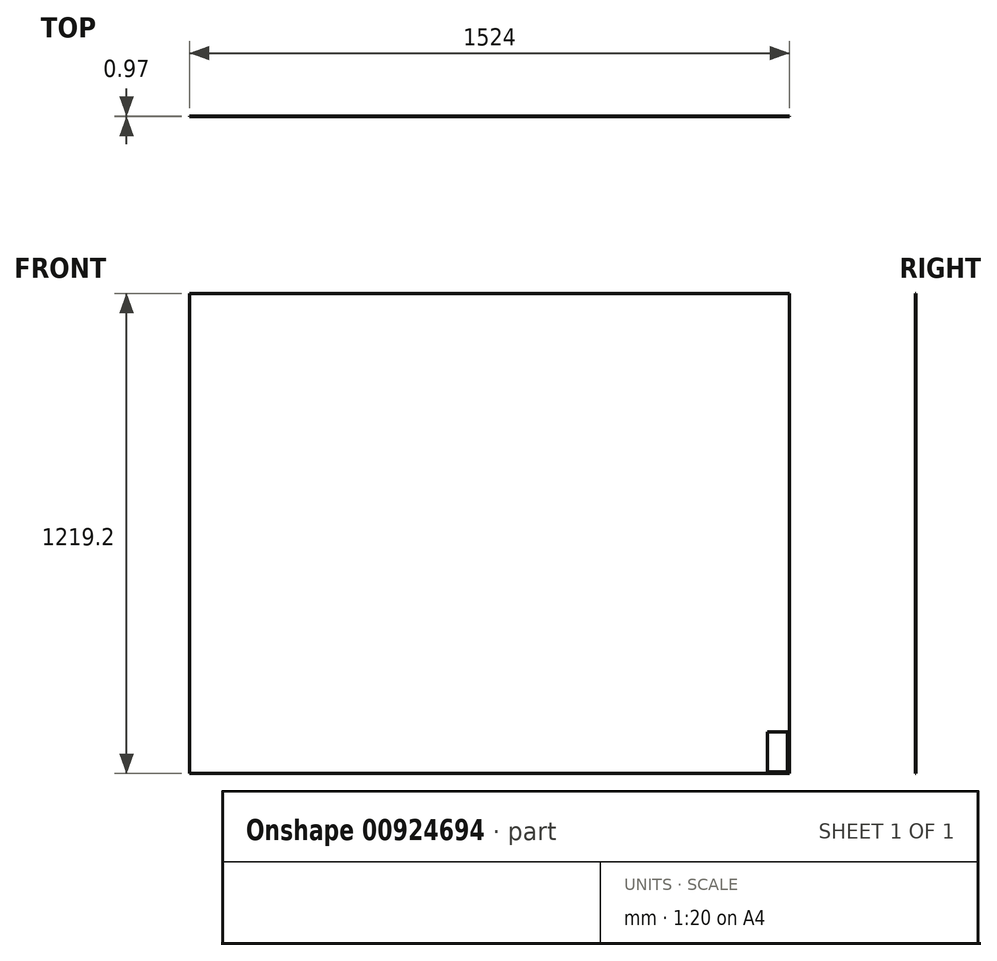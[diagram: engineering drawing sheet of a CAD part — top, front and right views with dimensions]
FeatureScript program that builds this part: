
annotation { "Feature Type Name" : "Feature", "Feature Type Description" : "" }
export const myFeature = defineFeature(function(context is Context, id is Id, definition is map)
    precondition{}
    {
        {
            var Q0;
            Q0=qCreatedBy(makeId("Front.planeOp"),FACE);
            var sketch = newSketch(context, id + "F0", { "sketchPlane" : qUnion([Q0])});
            skLineSegment(sketch, "E0.bottom", {"start": v(-1521.28, 1219.29) * mm, "end": v(2.72, 1219.29) * mm});
            skLineSegment(sketch, "E0.top", {"start": v(-1521.28, 0.09) * mm, "end": v(2.72, 0.09) * mm});
            skLineSegment(sketch, "E0.left", {"start": v(-1521.28, 1219.29) * mm, "end": v(-1521.28, 0.09) * mm});
            skLineSegment(sketch, "E0.right", {"start": v(2.72, 1219.29) * mm, "end": v(2.72, 0.09) * mm});
            skSolve(sketch);
        }
        {
            var Q0;
            Q0=makeQuery(id+"F0.imprint","IMPRINT",FACE,{"disambiguationData":[TD([[makeQuery(id+"F0.imprint","IMPRINT",EDGE,{"derivedFrom":sQuery(id+"F0.wireOp",EDGE,"E0.bottom")}),-1.0]])]});
            var sketch = newSketch(context, id + "F1", { "sketchPlane" : qUnion([Q0])});
            skLineSegment(sketch, "E1.bottom", {"start": v(-52.72, 105.7) * mm, "end": v(-1.92, 105.7) * mm});
            skLineSegment(sketch, "E1.top", {"start": v(-52.72, 4.1) * mm, "end": v(-1.92, 4.1) * mm});
            skLineSegment(sketch, "E1.left", {"start": v(-52.72, 105.7) * mm, "end": v(-52.72, 4.1) * mm});
            skLineSegment(sketch, "E1.right", {"start": v(-1.92, 105.7) * mm, "end": v(-1.92, 4.1) * mm});
            skSolve(sketch);
        }
        {
            var Q0;
            Q0=makeQuery(id+"F0.imprint","IMPRINT",FACE,{"disambiguationData":[TD([[makeQuery(id+"F0.imprint","IMPRINT",EDGE,{"derivedFrom":sQuery(id+"F0.wireOp",EDGE,"E0.bottom")}),-1.0]])]});
            extrude(context, id + "F2", {"entities" : qUnion([Q0]), "depth" : 0.97 * mm, "offsetDistance" : 25.4 * mm});
        }
        {
            var Q0;
            Q0 = qSketchRegion(id + "F1", true);
            extrude(context, id + "F3", {"entities" : qUnion([Q0]), "depth" : 0.97 * mm, "offsetDistance" : 25.4 * mm});
        }
    });
